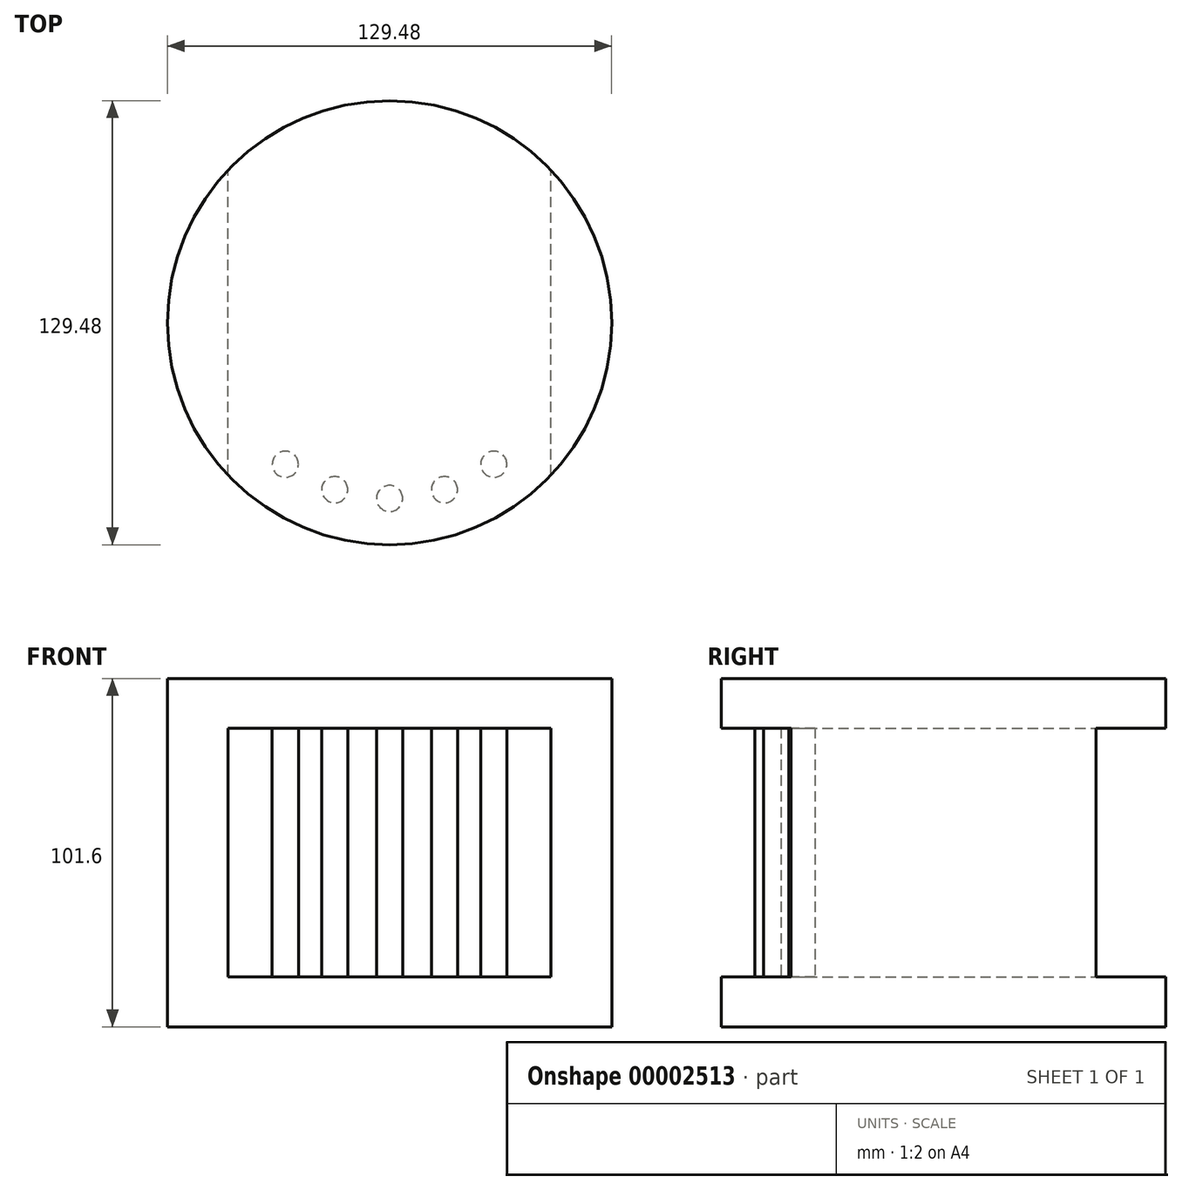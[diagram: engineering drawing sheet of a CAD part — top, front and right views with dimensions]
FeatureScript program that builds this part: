
annotation { "Feature Type Name" : "Feature", "Feature Type Description" : "" }
export const myFeature = defineFeature(function(context is Context, id is Id, definition is map)
    precondition{}
    {
        {
            var Q0;
            Q0=qCreatedBy(makeId("Top.planeOp"),FACE);
            var sketch = newSketch(context, id + "F0", { "sketchPlane" : qUnion([Q0])});
            skCircle(sketch, "E0", {"center": v(0, 0) * mm, "radius": 64.74 * mm});
            skSolve(sketch);
        }
        {
            var Q0;
            Q0 = qSketchRegion(id + "F0", true);
            extrude(context, id + "F1", {"entities" : qUnion([Q0]), "depth" : 101.6 * mm});
        }
        {
            var Q0;
            Q0=qCreatedBy(makeId("Front.planeOp"),FACE);
            var sketch = newSketch(context, id + "F2", { "sketchPlane" : qUnion([Q0])});
            skLineSegment(sketch, "E1.bottom", {"start": v(47.05, 14.55) * mm, "end": v(-47.05, 14.55) * mm});
            skLineSegment(sketch, "E1.top", {"start": v(47.05, 87.1) * mm, "end": v(-47.05, 87.1) * mm});
            skLineSegment(sketch, "E1.left", {"start": v(47.05, 14.55) * mm, "end": v(47.05, 87.1) * mm});
            skLineSegment(sketch, "E1.right", {"start": v(-47.05, 14.55) * mm, "end": v(-47.05, 87.1) * mm});
            skPoint(sketch, "E1.middle", {"position": v(0, 50.82) * mm});
            skSolve(sketch);
        }
        {
            var Q0;
            Q0 = qSketchRegion(id + "F2", true);
            extrude(context, id + "F3", {"entities" : qUnion([Q0]), "operationType" : NewBodyOperationType.REMOVE, "endBound" : BoundingType.SYMMETRIC, "depth" : 254 * mm});
        }
        {
            var Q0;
            Q0=makeQuery(id+"F3.boolean.opBoolean","COPY",FACE,{"derivedFrom":makeQuery(id+"F3.opExtrude","SWEPT_FACE",FACE,{"disambiguationData":[OSD([sQuery(id+"F2.wireOp",EDGE,"E1.bottom")])]})});
            var sketch = newSketch(context, id + "F4", { "sketchPlane" : qUnion([Q0])});
            skCircle(sketch, "E2", {"center": v(-30.38, -41.28) * mm, "radius": 3.82 * mm});
            skCircle(sketch, "E3", {"center": v(-15.99, -48.7) * mm, "radius": 3.82 * mm});
            skCircle(sketch, "E4", {"center": v(0, -51.25) * mm, "radius": 3.82 * mm});
            skCircle(sketch, "E5", {"center": v(15.99, -48.7) * mm, "radius": 3.82 * mm});
            skCircle(sketch, "E6", {"center": v(30.38, -41.28) * mm, "radius": 3.82 * mm});
            skCircle(sketch, "E7", {"center": v(0, 0) * mm, "radius": 51.25 * mm, "construction": true});
            skLineSegment(sketch, "E8", {"start": v(-30.38, -41.28) * mm, "end": v(-15.99, -48.7) * mm, "construction": true});
            skLineSegment(sketch, "E9", {"start": v(-15.99, -48.7) * mm, "end": v(0, -51.25) * mm, "construction": true});
            skLineSegment(sketch, "E10", {"start": v(0, -51.25) * mm, "end": v(15.99, -48.7) * mm, "construction": true});
            skLineSegment(sketch, "E11", {"start": v(15.99, -48.7) * mm, "end": v(30.38, -41.28) * mm, "construction": true});
            skSolve(sketch);
        }
        {
            var Q0;
            Q0 = qSketchRegion(id + "F4", true);
            var Q1;
            Q1=makeQuery(id+"F3.boolean.opBoolean","COPY",FACE,{"derivedFrom":makeQuery(id+"F3.opExtrude","SWEPT_FACE",FACE,{"disambiguationData":[OSD([sQuery(id+"F2.wireOp",EDGE,"E1.top")])]})});
            extrude(context, id + "F5", {"entities" : qUnion([Q0]), "operationType" : NewBodyOperationType.ADD, "endBound" : BoundingType.UP_TO_SURFACE, "endBoundEntityFace" : qUnion([Q1]), "depth" : 25.4 * mm});
        }
        {
            var Q0;
            Q0=makeQuery(id+"F3.boolean.opBoolean","COPY",FACE,{"derivedFrom":makeQuery(id+"F3.opExtrude","SWEPT_FACE",FACE,{"disambiguationData":[OSD([sQuery(id+"F2.wireOp",EDGE,"E1.right")])]})});
            var Q1;
            Q1=makeQuery(id+"F3.boolean.opBoolean","COPY",FACE,{"derivedFrom":makeQuery(id+"F3.opExtrude","SWEPT_FACE",FACE,{"disambiguationData":[OSD([sQuery(id+"F2.wireOp",EDGE,"E1.bottom")])]})});
            cPlane(context, id + "F6", {"entities" : qUnion([Q0, Q1]), "cplaneType" : CPlaneType.MID_PLANE, "offset" : 101.6 * mm, "width" : 152.4 * mm, "height" : 152.4 * mm});
        }
    });
